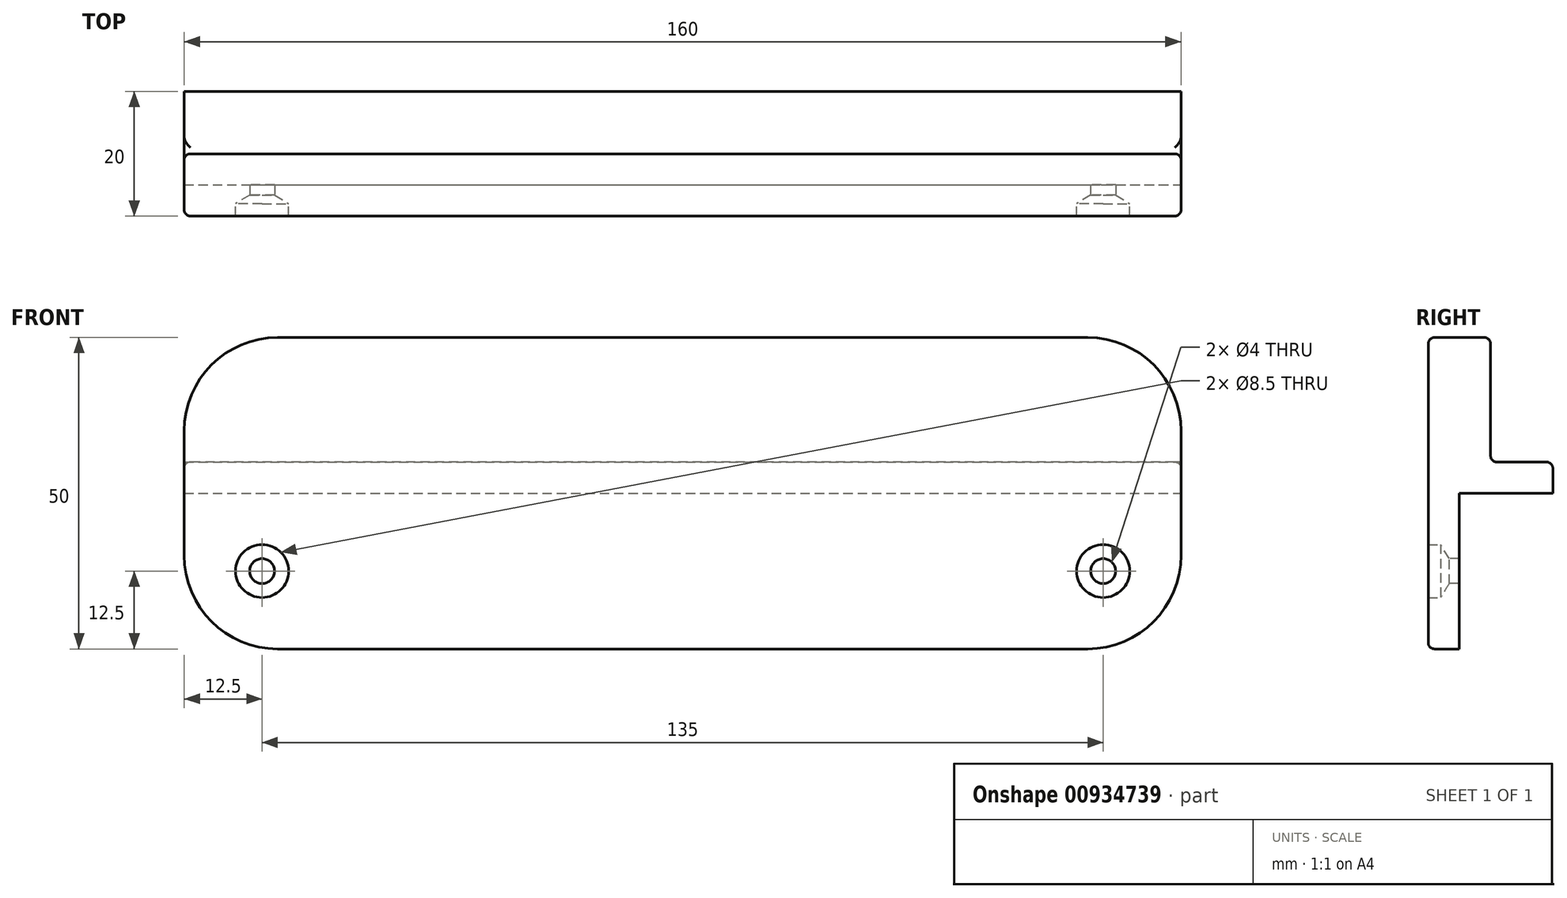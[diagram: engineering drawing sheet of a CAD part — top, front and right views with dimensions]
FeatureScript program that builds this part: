
annotation { "Feature Type Name" : "Feature", "Feature Type Description" : "" }
export const myFeature = defineFeature(function(context is Context, id is Id, definition is map)
    precondition{}
    {
        {
            var Q0;
            Q0=qCreatedBy(makeId("Top.planeOp"),FACE);
            var sketch = newSketch(context, id + "F0", { "sketchPlane" : qUnion([Q0])});
            skLineSegment(sketch, "E0", {"start": v(0, 0) * mm, "end": v(160, 0) * mm});
            skLineSegment(sketch, "E1", {"start": v(160, 5) * mm, "end": v(160, 0) * mm});
            skLineSegment(sketch, "E2", {"start": v(160, 5) * mm, "end": v(160, 10) * mm});
            skLineSegment(sketch, "E3", {"start": v(160, 10) * mm, "end": v(0, 10) * mm});
            skLineSegment(sketch, "E4", {"start": v(0, 10) * mm, "end": v(0, 5) * mm});
            skLineSegment(sketch, "E5", {"start": v(0, 5) * mm, "end": v(0, 0) * mm});
            skLineSegment(sketch, "E6", {"start": v(0, 5) * mm, "end": v(160, 5) * mm});
            skLineSegment(sketch, "E7", {"start": v(0, 10) * mm, "end": v(0, 20) * mm});
            skLineSegment(sketch, "E8", {"start": v(0, 20) * mm, "end": v(160, 20) * mm});
            skLineSegment(sketch, "E9", {"start": v(160, 20) * mm, "end": v(160, 10) * mm});
            skSolve(sketch);
        }
        {
            var Q0;
            Q0=makeQuery(id+"F0.imprint","IMPRINT",FACE,{"disambiguationData":[TD([[makeQuery(id+"F0.imprint","IMPRINT",EDGE,{"derivedFrom":sQuery(id+"F0.wireOp",EDGE,"E0")}),1.0]])]});
            var Q1;
            Q1=makeQuery(id+"F0.imprint","IMPRINT",FACE,{"disambiguationData":[TD([[makeQuery(id+"F0.imprint","IMPRINT",EDGE,{"derivedFrom":sQuery(id+"F0.wireOp",EDGE,"E2")}),1.0]])]});
            extrude(context, id + "F1", {"entities" : qUnion([Q0, Q1]), "depth" : 25 * mm, "offsetDistance" : 25 * mm});
        }
        {
            var Q0;
            Q0=makeQuery(id+"F0.imprint","IMPRINT",FACE,{"disambiguationData":[TD([[makeQuery(id+"F0.imprint","IMPRINT",EDGE,{"derivedFrom":sQuery(id+"F0.wireOp",EDGE,"E3")}),-1.0]])]});
            extrude(context, id + "F2", {"entities" : qUnion([Q0]), "operationType" : NewBodyOperationType.ADD, "depth" : 5 * mm, "offsetDistance" : 25 * mm});
        }
        {
            var Q0;
            Q0=makeQuery(id+"F0.imprint","IMPRINT",FACE,{"disambiguationData":[TD([[makeQuery(id+"F0.imprint","IMPRINT",EDGE,{"derivedFrom":sQuery(id+"F0.wireOp",EDGE,"E0")}),1.0]])]});
            extrude(context, id + "F3", {"entities" : qUnion([Q0]), "operationType" : NewBodyOperationType.ADD, "oppositeDirection" : true, "depth" : 25 * mm, "offsetDistance" : 25 * mm});
        }
        {
            var Q0;
            {var subQ0=sQuery(id+"F0.wireOp",EDGE,"E0");Q0=makeQuery(id+"F3.boolean.opBoolean","MERGE",FACE,{"derivedFrom":[makeQuery(id+"F1.opExtrude","SWEPT_FACE",FACE,{"disambiguationData":[OSD([subQ0])]}),makeQuery(id+"F3.opExtrude","SWEPT_FACE",FACE,{"disambiguationData":[OSD([subQ0])]})]});}
            var sketch = newSketch(context, id + "F4", { "sketchPlane" : qUnion([Q0])});
            skLineSegment(sketch, "E10", {"start": v(0, -25) * mm, "end": v(0, -12.5) * mm, "construction": true});
            skLineSegment(sketch, "E11", {"start": v(0, -12.5) * mm, "end": v(0, 0) * mm, "construction": true});
            skLineSegment(sketch, "E12", {"start": v(0, -12.5) * mm, "end": v(12.5, -12.5) * mm, "construction": true});
            skLineSegment(sketch, "E13", {"start": v(160, -12.5) * mm, "end": v(147.5, -12.5) * mm, "construction": true});
            skCircle(sketch, "E14", {"center": v(12.5, -12.5) * mm, "radius": 2 * mm});
            skCircle(sketch, "E15", {"center": v(147.5, -12.5) * mm, "radius": 2 * mm});
            skSolve(sketch);
        }
        {
            var Q0;
            Q0=makeQuery(id+"F4.imprint","IMPRINT",FACE,{"disambiguationData":[TD([[makeQuery(id+"F4.imprint","IMPRINT",EDGE,{"derivedFrom":sQuery(id+"F4.wireOp",EDGE,"E14")}),1.0]])]});
            var Q1;
            Q1=makeQuery(id+"F4.imprint","IMPRINT",FACE,{"disambiguationData":[TD([[makeQuery(id+"F4.imprint","IMPRINT",EDGE,{"derivedFrom":sQuery(id+"F4.wireOp",EDGE,"E15")}),1.0]])]});
            extrude(context, id + "F5", {"entities" : qUnion([Q0, Q1]), "operationType" : NewBodyOperationType.REMOVE, "endBound" : BoundingType.UP_TO_NEXT, "oppositeDirection" : true, "depth" : 25 * mm, "offsetDistance" : 25 * mm});
        }
        {
            var Q0;
            Q0=sQuery(id+"F4.wireOp",VERTEX,"E12.end");
            var Q1;
            Q1=sQuery(id+"F4.wireOp",VERTEX,"E13.end");
            var Q2;
            Q2=makeQuery(id+"F1.opExtrude","SWEPT_BODY",BODY,{"disambiguationData":[OSD([sQuery(id+"F0.wireOp",EDGE,"E0"),sQuery(id+"F0.wireOp",EDGE,"E1"),sQuery(id+"F0.wireOp",EDGE,"E2"),sQuery(id+"F0.wireOp",EDGE,"E3"),sQuery(id+"F0.wireOp",EDGE,"E4"),sQuery(id+"F0.wireOp",EDGE,"E5")])]});
            hole(context, id + "F6", {"style" : HoleStyle.SIMPLE, "endStyle" : HoleEndStyle.BLIND, "holeDiameter" : 8.5 * mm, "majorDiameter" : 5 * mm, "holeDepth" : 2 * mm, "isTappedThrough" : true, "tappedDepth" : 12 * mm, "tapClearance" : 3, "locations" : qUnion([Q0, Q1]), "scope" : qUnion([Q2])});
        }
        {
            var Q0;
            Q0=makeQuery(id+"F3.opExtrude","CAP_EDGE",EDGE,{"disambiguationData":[OSD([sQuery(id+"F0.wireOp",EDGE,"E1")])],"isStart":false});
            var Q1;
            Q1=makeQuery(id+"F3.opExtrude","CAP_EDGE",EDGE,{"disambiguationData":[OSD([sQuery(id+"F0.wireOp",EDGE,"E5")])],"isStart":false});
            var Q2;
            Q2=makeQuery(id+"F1.opExtrude","CAP_EDGE",EDGE,{"disambiguationData":[OSD([sQuery(id+"F0.wireOp",EDGE,"E1"),sQuery(id+"F0.wireOp",EDGE,"E2")])],"isStart":false});
            var Q3;
            Q3=makeQuery(id+"F1.opExtrude","CAP_EDGE",EDGE,{"disambiguationData":[OSD([sQuery(id+"F0.wireOp",EDGE,"E4"),sQuery(id+"F0.wireOp",EDGE,"E5")])],"isStart":false});
            fillet(context, id + "F7", {"entities" : qUnion([Q0, Q1, Q2, Q3]), "radius" : 15 * mm, "tangentPropagation" : true, "allowEdgeOverflow" : false});
        }
        {
            var Q0;
            Q0=makeQuery(id+"F1.opExtrude","SWEPT_FACE",FACE,{"disambiguationData":[OSD([sQuery(id+"F0.wireOp",EDGE,"E3")])]});
            var Q1;
            Q1=makeQuery(id+"F1.opExtrude","CAP_EDGE",EDGE,{"disambiguationData":[OSD([sQuery(id+"F0.wireOp",EDGE,"E0")])],"isStart":false});
            var Q2;
            Q2=makeQuery(id+"F2.opExtrude","CAP_EDGE",EDGE,{"disambiguationData":[OSD([sQuery(id+"F0.wireOp",EDGE,"E8")])],"isStart":false});
            fillet(context, id + "F8", {"entities" : qUnion([Q0, Q1, Q2]), "radius" : 1 * mm, "tangentPropagation" : true, "allowEdgeOverflow" : false});
        }
    });
